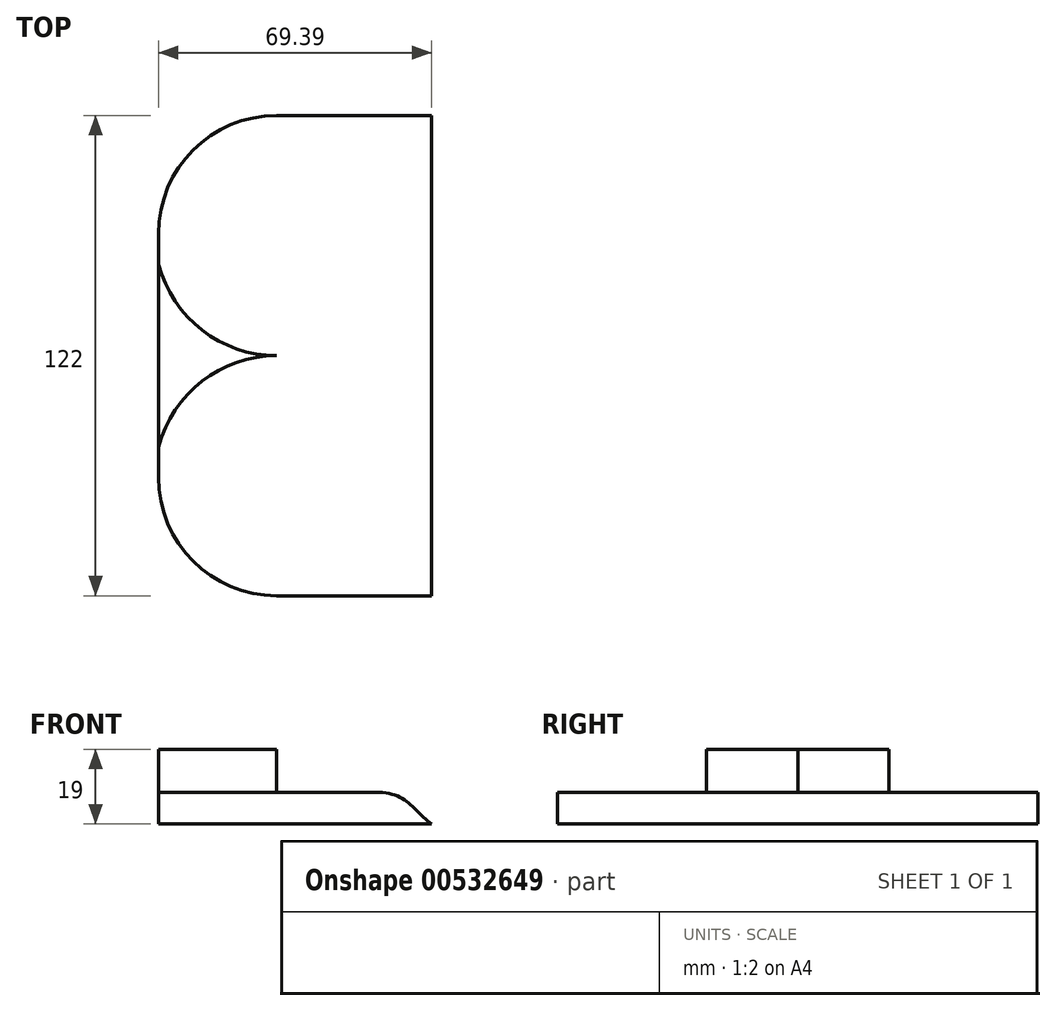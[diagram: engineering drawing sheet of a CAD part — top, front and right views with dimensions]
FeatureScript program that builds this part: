
annotation { "Feature Type Name" : "Feature", "Feature Type Description" : "" }
export const myFeature = defineFeature(function(context is Context, id is Id, definition is map)
    precondition{}
    {
        {
            var Q0;
            Q0=qCreatedBy(makeId("Front.planeOp"),FACE);
            var sketch = newSketch(context, id + "F0", { "sketchPlane" : qUnion([Q0])});
            skLineSegment(sketch, "E0", {"start": v(-69, 5) * mm, "end": v(-13, 5) * mm});
            skFitSpline(sketch, "E1", {"points": [v(-13, 5) * mm, v(-3, 0) * mm, v(7, -5) * mm], "startDerivative": vector(30, 0) * mm, "endDerivative": vector(30, 0) * mm});
            skPoint(sketch, "E2.end.orphan", {"position": v(-3, -5) * mm});
            skLineSegment(sketch, "E3", {"start": v(-69, -3) * mm, "end": v(0.39, -3) * mm});
            skLineSegment(sketch, "E4", {"start": v(-69, 5) * mm, "end": v(-69, -3) * mm});
            skPoint(sketch, "E5.orphan", {"position": v(-74.47, -3) * mm});
            skPoint(sketch, "E6.end.orphan", {"position": v(-3, 5) * mm});
            skSolve(sketch);
        }
        {
            var Q0;
            Q0 = qSketchRegion(id + "F0", true);
            extrude(context, id + "F1", {"entities" : qUnion([Q0]), "depth" : 122 * mm, "offsetDistance" : 25 * mm});
        }
        {
            var Q0;
            Q0=makeQuery(id+"F1.opExtrude","SWEPT_FACE",FACE,{"disambiguationData":[OSD([sQuery(id+"F0.wireOp",EDGE,"E0")])]});
            var sketch = newSketch(context, id + "F2", { "sketchPlane" : qUnion([Q0])});
            skArc(sketch, "E7", {"start": v(-39, -61) * mm, "mid": v(-57.96, -67.47) * mm, "end": v(-69, -84.19) * mm});
            skArc(sketch, "E8", {"start": v(-69, -37.81) * mm, "mid": v(-57.96, -54.53) * mm, "end": v(-39, -61) * mm});
            skLineSegment(sketch, "E9", {"start": v(-69, -84.19) * mm, "end": v(-69, -37.81) * mm});
            skSolve(sketch);
        }
        {
            var Q0;
            Q0 = qSketchRegion(id + "F2", true);
            extrude(context, id + "F3", {"entities" : qUnion([Q0]), "operationType" : NewBodyOperationType.ADD, "depth" : 11 * mm, "offsetDistance" : 25 * mm});
        }
        {
            var Q0;
            Q0=makeQuery(id+"F1.opExtrude","SWEPT_FACE",FACE,{"disambiguationData":[OSD([sQuery(id+"F0.wireOp",EDGE,"E0")])]});
            var sketch = newSketch(context, id + "F4", { "sketchPlane" : qUnion([Q0])});
            skArc(sketch, "E10", {"start": v(-69, -92) * mm, "mid": v(-60.21, -113.21) * mm, "end": v(-39, -122) * mm});
            skArc(sketch, "E11", {"start": v(-69, -30) * mm, "mid": v(-60.21, -8.79) * mm, "end": v(-39, 0) * mm});
            skLineSegment(sketch, "E12", {"start": v(-39, -122) * mm, "end": v(-69, -122) * mm});
            skLineSegment(sketch, "E13", {"start": v(-69, -122) * mm, "end": v(-69, -92) * mm});
            skLineSegment(sketch, "E14", {"start": v(-69, -30) * mm, "end": v(-69, 0) * mm});
            skLineSegment(sketch, "E15", {"start": v(-69, 0) * mm, "end": v(-39, 0) * mm});
            skSolve(sketch);
        }
        {
            var Q0;
            Q0 = qSketchRegion(id + "F4", true);
            extrude(context, id + "F5", {"entities" : qUnion([Q0]), "operationType" : NewBodyOperationType.REMOVE, "endBound" : BoundingType.THROUGH_ALL, "oppositeDirection" : true, "depth" : 25 * mm, "offsetDistance" : 25 * mm});
        }
    });
